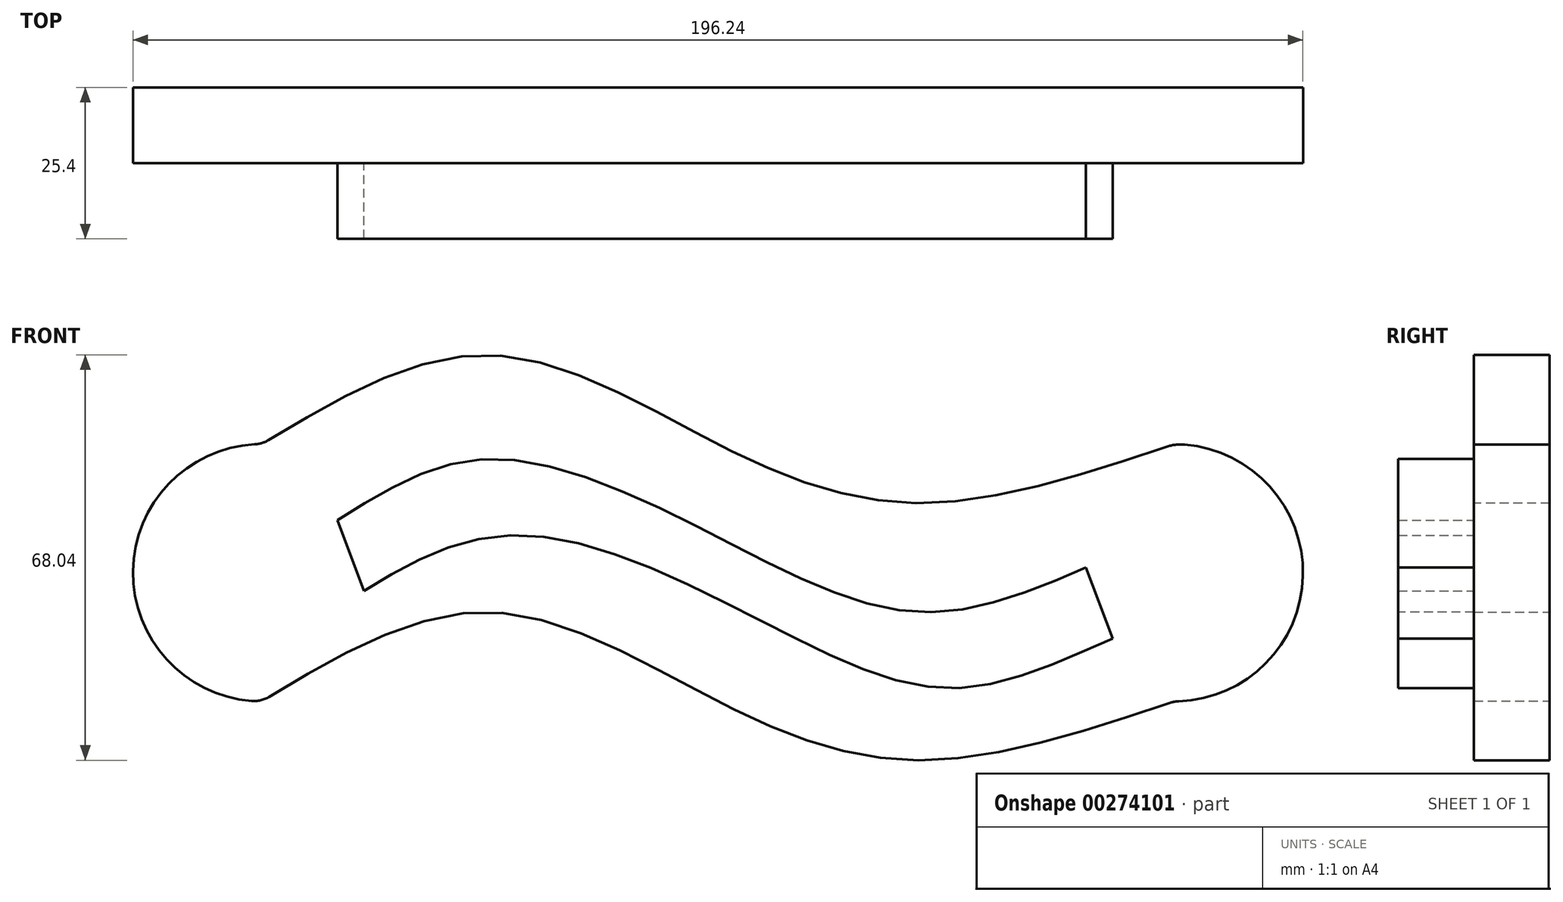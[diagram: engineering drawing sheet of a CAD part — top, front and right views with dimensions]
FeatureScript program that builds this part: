
annotation { "Feature Type Name" : "Feature", "Feature Type Description" : "" }
export const myFeature = defineFeature(function(context is Context, id is Id, definition is map)
    precondition{}
    {
        {
            var Q0;
            Q0=qCreatedBy(makeId("Front.planeOp"),FACE);
            var sketch = newSketch(context, id + "F0", { "sketchPlane" : qUnion([Q0])});
            skLineSegment(sketch, "E0", {"start": v(-76.53, 20.73) * mm, "end": v(-76.53, -22.45) * mm});
            skLineSegment(sketch, "E1", {"start": v(76.53, 20.73) * mm, "end": v(76.53, -22.45) * mm});
            skFitSpline(sketch, "E2", {"points": [v(-76.53, 20.73) * mm, v(-38.27, 35.7) * mm, v(0, 20.73) * mm, v(33.7, 10.85) * mm, v(76.53, 20.73) * mm], "startDerivative": vector(150.62, 90.9) * mm, "endDerivative": vector(169.99, 56.98) * mm});
            skFitSpline(sketch, "E3", {"points": [v(-76.53, -22.45) * mm, v(-38.27, -7.48) * mm, v(0, -22.45) * mm, v(33.7, -32.33) * mm, v(76.53, -22.45) * mm], "startDerivative": vector(150.62, 90.9) * mm, "endDerivative": vector(169.99, 56.98) * mm});
            skArc(sketch, "E4", {"start": v(76.53, -22.45) * mm, "mid": v(98.12, -0.86) * mm, "end": v(76.53, 20.73) * mm});
            skArc(sketch, "E5", {"start": v(-76.53, 20.73) * mm, "mid": v(-98.12, -0.86) * mm, "end": v(-76.53, -22.45) * mm});
            skFitSpline(sketch, "E6", {"points": [v(-63.85, 7.97) * mm, v(-38.27, 18.25) * mm, v(0, 5.12) * mm, v(33.7, -7.45) * mm, v(61.73, 0) * mm], "startDerivative": vector(105.16, 66.18) * mm, "endDerivative": vector(118.35, 50.49) * mm});
            skFitSpline(sketch, "E7", {"points": [v(-59.37, -3.91) * mm, v(-33.44, 5.45) * mm, v(4.83, -7.68) * mm, v(38.52, -20.25) * mm, v(66.2, -11.88) * mm], "startDerivative": vector(105.16, 66.18) * mm, "endDerivative": vector(118.35, 50.49) * mm});
            skLineSegment(sketch, "E8", {"start": v(-63.85, 7.97) * mm, "end": v(-59.37, -3.91) * mm});
            skLineSegment(sketch, "E9", {"start": v(61.73, 0) * mm, "end": v(66.2, -11.88) * mm});
            skSolve(sketch);
        }
        {
            var Q0;
            Q0 = qSketchRegion(id + "F0", true);
            extrude(context, id + "F1", {"entities" : qUnion([Q0]), "depth" : 12.7 * mm});
        }
        {
            var Q0;
            Q0=makeQuery(id+"F0.imprint","IMPRINT",FACE,{"disambiguationData":[TD([[makeQuery(id+"F0.imprint","IMPRINT",EDGE,{"derivedFrom":sQuery(id+"F0.wireOp",EDGE,"E6")}),-1.0]])]});
            extrude(context, id + "F2", {"entities" : qUnion([Q0]), "operationType" : NewBodyOperationType.ADD, "depth" : 25.4 * mm});
        }
        {
            var Q0;
            Q0=makeQuery(id+"F1.opExtrude","SWEPT_EDGE",EDGE,{"disambiguationData":[OSD([sQuery(id+"F0.wireOp",EDGE,"E1"),sQuery(id+"F0.wireOp",EDGE,"E2"),sQuery(id+"F0.wireOp",EDGE,"E4")])]});
            fillet(context, id + "F3", {"entities" : qUnion([Q0]), "radius" : 7.62 * mm, "tangentPropagation" : true, "allowEdgeOverflow" : false});
        }
        {
            var Q0;
            Q0=makeQuery(id+"F1.opExtrude","SWEPT_EDGE",EDGE,{"disambiguationData":[OSD([sQuery(id+"F0.wireOp",EDGE,"E0"),sQuery(id+"F0.wireOp",EDGE,"E3"),sQuery(id+"F0.wireOp",EDGE,"E5")])]});
            fillet(context, id + "F4", {"entities" : qUnion([Q0]), "radius" : 5.08 * mm, "tangentPropagation" : true, "allowEdgeOverflow" : false});
        }
        {
            var Q0;
            Q0=makeQuery(id+"F1.opExtrude","SWEPT_EDGE",EDGE,{"disambiguationData":[OSD([sQuery(id+"F0.wireOp",EDGE,"E0"),sQuery(id+"F0.wireOp",EDGE,"E2"),sQuery(id+"F0.wireOp",EDGE,"E5")])]});
            fillet(context, id + "F5", {"entities" : qUnion([Q0]), "radius" : 5.08 * mm, "tangentPropagation" : true, "allowEdgeOverflow" : false});
        }
        {
            var Q0;
            Q0=makeQuery(id+"F1.opExtrude","SWEPT_EDGE",EDGE,{"disambiguationData":[OSD([sQuery(id+"F0.wireOp",EDGE,"E1"),sQuery(id+"F0.wireOp",EDGE,"E3"),sQuery(id+"F0.wireOp",EDGE,"E4")])]});
            fillet(context, id + "F6", {"entities" : qUnion([Q0]), "radius" : 5.08 * mm, "tangentPropagation" : true, "allowEdgeOverflow" : false});
        }
        {
            var Q0;
            Q0=qCreatedBy(makeId("Top.planeOp"),FACE);
            var sketch = newSketch(context, id + "F7", { "sketchPlane" : qUnion([Q0])});
            skLineSegment(sketch, "E10.bottom", {"start": v(0, 0) * mm, "end": v(2.54, 0) * mm});
            skLineSegment(sketch, "E10.top", {"start": v(0, 12.7) * mm, "end": v(2.54, 12.7) * mm});
            skLineSegment(sketch, "E10.left", {"start": v(0, 0) * mm, "end": v(0, 12.7) * mm});
            skLineSegment(sketch, "E10.right", {"start": v(2.54, 0) * mm, "end": v(2.54, 12.7) * mm});
            skLineSegment(sketch, "E11.bottom", {"start": v(75.7, 0) * mm, "end": v(78.25, 0) * mm});
            skLineSegment(sketch, "E11.top", {"start": v(75.7, 12.7) * mm, "end": v(78.25, 12.7) * mm});
            skLineSegment(sketch, "E11.left", {"start": v(75.7, 0) * mm, "end": v(75.7, 12.7) * mm});
            skLineSegment(sketch, "E11.right", {"start": v(78.25, 0) * mm, "end": v(78.25, 12.7) * mm});
            skLineSegment(sketch, "E12.bottom", {"start": v(-76.4, 0) * mm, "end": v(-73.85, 0) * mm});
            skLineSegment(sketch, "E12.top", {"start": v(-76.4, 12.7) * mm, "end": v(-73.85, 12.7) * mm});
            skLineSegment(sketch, "E12.left", {"start": v(-76.4, 0) * mm, "end": v(-76.4, 12.7) * mm});
            skLineSegment(sketch, "E12.right", {"start": v(-73.85, 0) * mm, "end": v(-73.85, 12.7) * mm});
            skSolve(sketch);
        }
        {
            var Q0;
            Q0 = qConstructionFilter(qBodyType(qCreatedBy(id + "F7" ,EDGE), BodyType.WIRE), ConstructionObject.NO);
            extrude(context, id + "F8", {"bodyType" : ToolBodyType.SURFACE, "surfaceEntities" : qUnion([Q0]), "depth" : 3.8 * mm});
        }
    });
